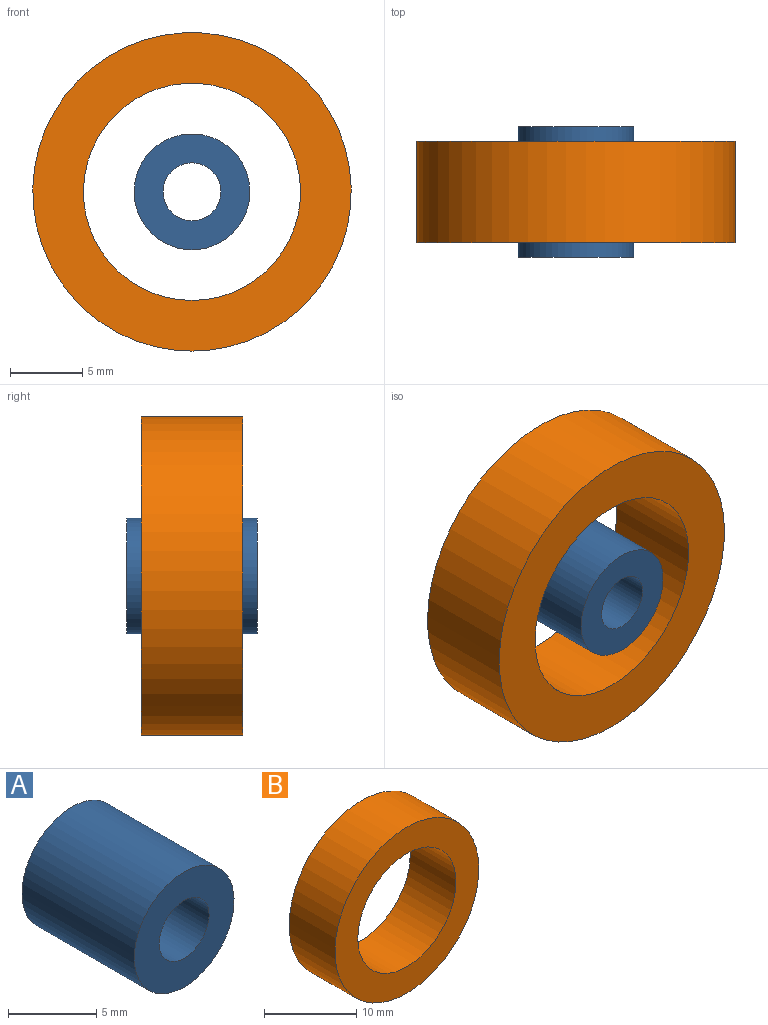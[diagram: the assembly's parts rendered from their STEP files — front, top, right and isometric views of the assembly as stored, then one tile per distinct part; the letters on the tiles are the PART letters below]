
ASSEMBLY  parts=2 mates=1
PART A: 4 faces, bbox 8x9x8 mm
  f0: cylinder r=2mm len=9mm, axis (0,1,0), area 113.1mm2, adj f2,f3
  f1: cylinder r=4mm len=9mm, axis (0,1,0), area 226.2mm2, adj f2,f3
  f2: plane 8x8mm, normal (0,-1,0), area 37.7mm2, adj f0,f1
  f3: plane 8x8mm, normal (0,1,0), area 37.7mm2, adj f0,f1
PART B: 4 faces, bbox 22x7x22 mm
  f0: cylinder r=7.5mm len=15mm, axis (0,1,0), area 329.9mm2, adj f2,f3
  f1: cylinder r=11mm len=22mm, axis (0,1,0), area 483.8mm2, adj f2,f3
  f2: plane 22x22mm, normal (0,-1,0), area 203.4mm2, adj f0,f1
  f3: plane 22x22mm, normal (0,1,0), area 203.4mm2, adj f0,f1
PLACE A t=(-7.08,-0.08,-0.74)mm
PLACE B t=(-7.08,-1.08,-0.74)mm
MATE fastened A.f0 <-> B.f0  axis (0,-1,0) through (-7.08,-9.08,-0.74)mm
